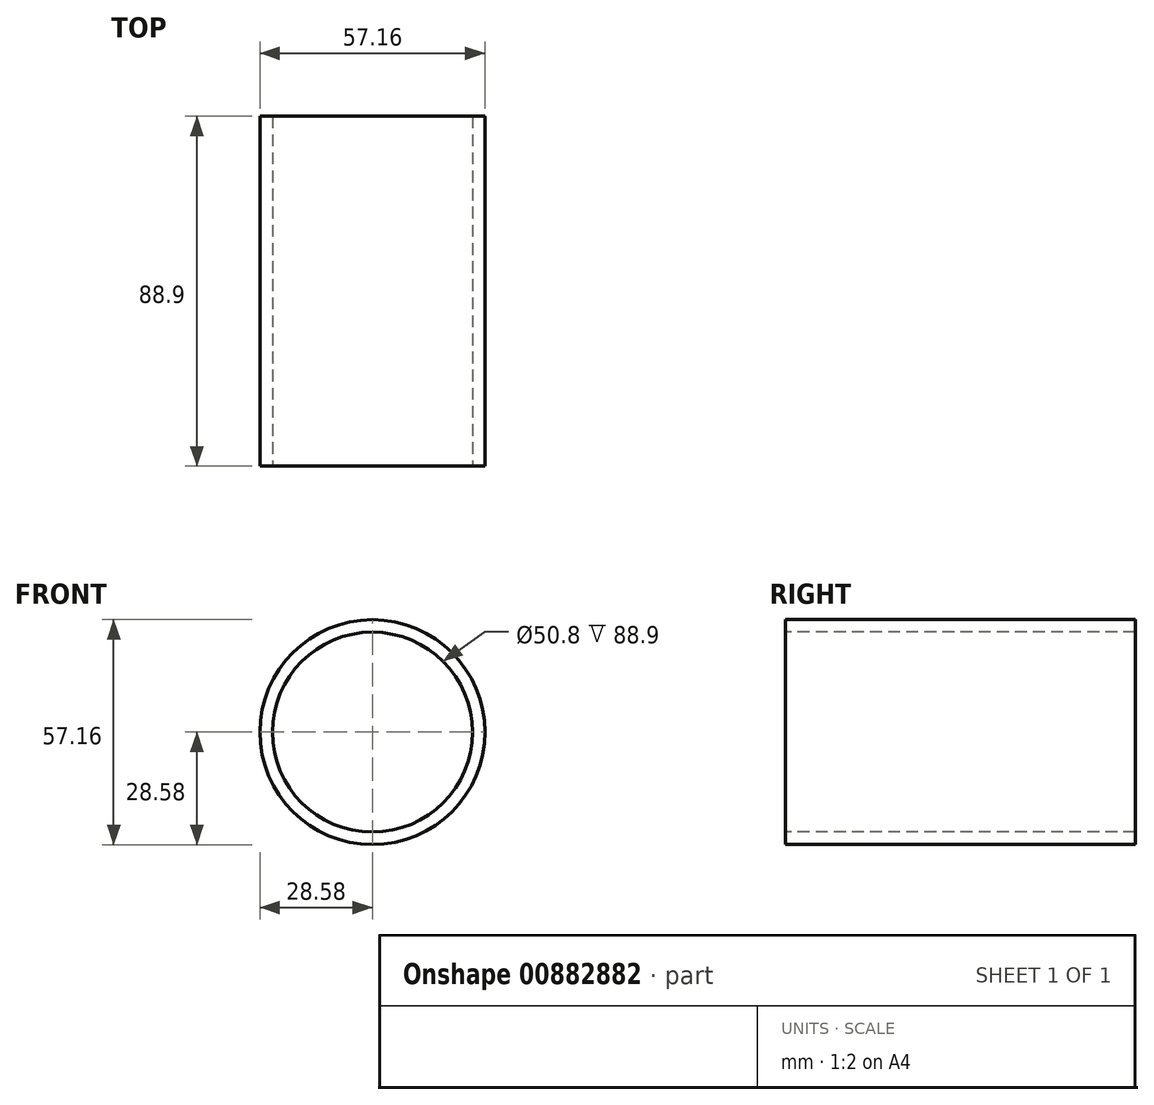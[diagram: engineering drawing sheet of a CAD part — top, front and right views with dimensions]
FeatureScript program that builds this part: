
annotation { "Feature Type Name" : "Feature", "Feature Type Description" : "" }
export const myFeature = defineFeature(function(context is Context, id is Id, definition is map)
    precondition{}
    {
        {
            var Q0;
            Q0=qCreatedBy(makeId("Front.planeOp"),FACE);
            var sketch = newSketch(context, id + "F0", { "sketchPlane" : qUnion([Q0])});
            skCircle(sketch, "E0", {"center": v(0, 0) * mm, "radius": 28.58 * mm});
            skCircle(sketch, "E1", {"center": v(0, 0) * mm, "radius": 25.4 * mm});
            skSolve(sketch);
        }
        {
            var Q0;
            Q0=makeQuery(id+"F0.imprint","IMPRINT",FACE,{"disambiguationData":[TD([[makeQuery(id+"F0.imprint","IMPRINT",EDGE,{"derivedFrom":sQuery(id+"F0.wireOp",EDGE,"E0")}),1.0]])]});
            extrude(context, id + "F1", {"entities" : qUnion([Q0]), "oppositeDirection" : true, "depth" : 88.9 * mm, "offsetDistance" : 25.4 * mm});
        }
    });
